# Revit family: Front_Load_Mailbox-Florence_Manufacturing-7High_Suite
name_source: partatom
category: Generic Models
revit_build: Autodesk Revit Architecture 2012 (Build: 20110916_2132(x64)
units: mm (PartAtom-declared; Revit-internal decimal feet)

## types (6) — shared parameters
Description = Front Load Mailbox
Door Material = Metal - Florence - Paint - Antique Bronze
Hardware = Metal - Florence - Steel
Height = 2' - 2 3/4"
Manufacturer = Florence Manufacturing
Minimum USPS Access Door = 3' - 0"
Mullion = 0' - 1 7/16"
Product Name = STD-4C
R Slot 3 = Empty
Unit Casing = Metal - Florence - Paint - Antique Bronze
Unit Casing Width = 2' - 1 13/16"
Width = 1' - 5"

## per-type parameters (varying)
| type | Center Mullion | Length | R Slot 1-Top | R Slot 2 | R Slot 4 | R Slot 5 | R Slot 6 | R Slot 7 | Side Frame Thickness | Slot 1-Top | Slot 2 | Slot 3 | Slot 4 | Slot 5 | Slot 6 | Slot 7 | URL |
| 4C07D-05 | Yes | 2' - 6 5/16" | Empty | Double Tenant Door | Letter Drop | Empty | Empty | Triple Tenant Door | 0' - 2 3/16" | Empty | Double Tenant Door | Empty | Double Tenant Door | Empty | Empty | Triple Tenant Door | http://www.florencemailboxes.com |
| 4C07S-1P | No | 1' - 4 1/4" | Empty | Empty | Empty | Empty | Empty | Empty | 0' - 2 5/16" | Vacant Tenant Door | Empty | Empty | Empty | Empty | Empty | Six High Single Parcel Locker |  |
| 4C07D-06 | Yes | 2' - 6 5/16" | Single Tenant Door | Single Tenant Door | Letter Drop | Single Tenant Door | Single Tenant Door | Single Tenant Door | 0' - 2 3/16" | Single Tenant Door | Empty | Empty | Empty | Empty | Empty | Six High Single Parcel Locker | http://www.florencemailboxes.com |
| 4C07D-12 | Yes | 2' - 6 5/16" | Single Tenant Door | Single Tenant Door | Letter Drop | Single Tenant Door | Single Tenant Door | Single Tenant Door | 0' - 2 3/16" | Single Tenant Door | Single Tenant Door | Single Tenant Door | Single Tenant Door | Single Tenant Door | Single Tenant Door | Single Tenant Door |  |
| 4C07S-05 | No | 1' - 4 1/4" | Empty | Empty | Empty | Empty | Empty | Empty | 0' - 2 5/16" | Single Tenant Door | Single Tenant Door | Empty | Letter Drop | Single Tenant Door | Single Tenant Door | Single Tenant Door |  |
| 4C07D-03 | Yes | 2' - 6 5/16" | Empty | Double Tenant Door | Letter Drop | Empty | Empty | Triple Tenant Door | 0' - 2 3/16" | Empty | Double Tenant Door | Empty | Empty | Empty | Empty | Five High Single Parcel Locker |  |

note: column(s) folded — value = type name in every type: Model

## geometry (parser evidence)
native form markers: Blend x2, Sweep x18
no freeform markers — native parametric forms only
